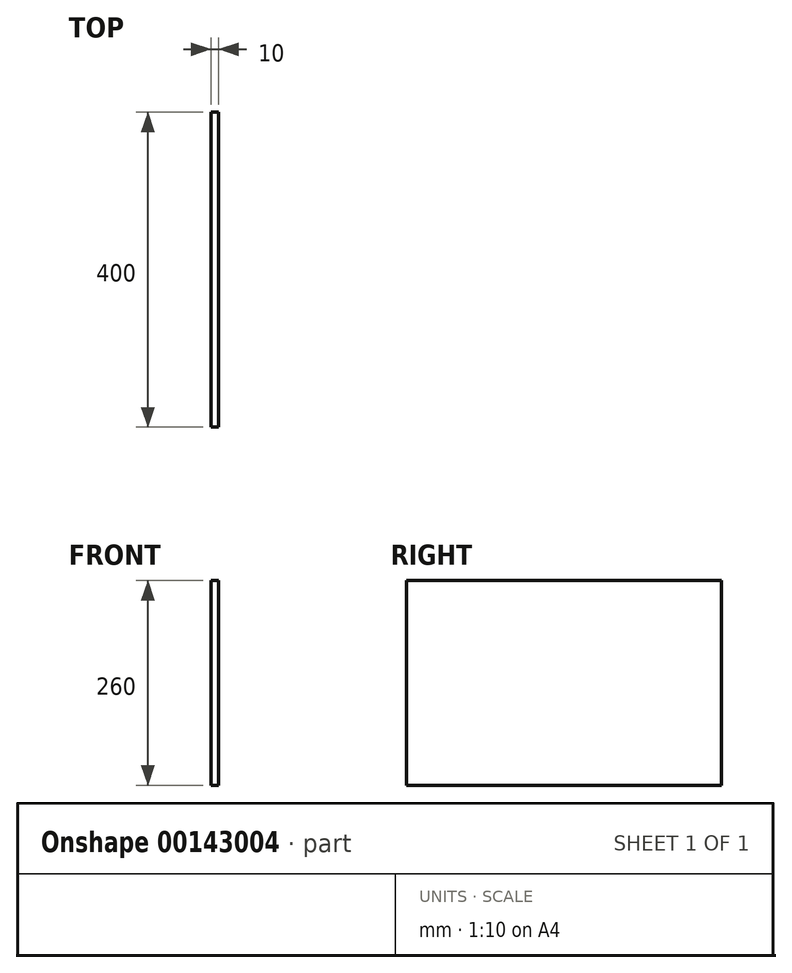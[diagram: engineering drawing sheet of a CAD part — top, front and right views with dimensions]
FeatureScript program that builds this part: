
annotation { "Feature Type Name" : "Feature", "Feature Type Description" : "" }
export const myFeature = defineFeature(function(context is Context, id is Id, definition is map)
    precondition{}
    {
        {
            var Q0;
            Q0=qCreatedBy(makeId("Right.planeOp"),FACE);
            var sketch = newSketch(context, id + "F0", { "sketchPlane" : qUnion([Q0])});
            skLineSegment(sketch, "E0.bottom", {"start": v(0, 0) * mm, "end": v(400, 0) * mm});
            skLineSegment(sketch, "E0.top", {"start": v(0, 260) * mm, "end": v(400, 260) * mm});
            skLineSegment(sketch, "E0.left", {"start": v(0, 0) * mm, "end": v(0, 260) * mm});
            skLineSegment(sketch, "E0.right", {"start": v(400, 0) * mm, "end": v(400, 260) * mm});
            skPoint(sketch, "E1.visualSharp", {"position": v(400, 0) * mm});
            skSolve(sketch);
        }
        {
            var Q0;
            Q0 = qSketchRegion(id + "F0", true);
            extrude(context, id + "F1", {"entities" : qUnion([Q0]), "depth" : 10 * mm, "offsetDistance" : 25 * mm});
        }
    });
